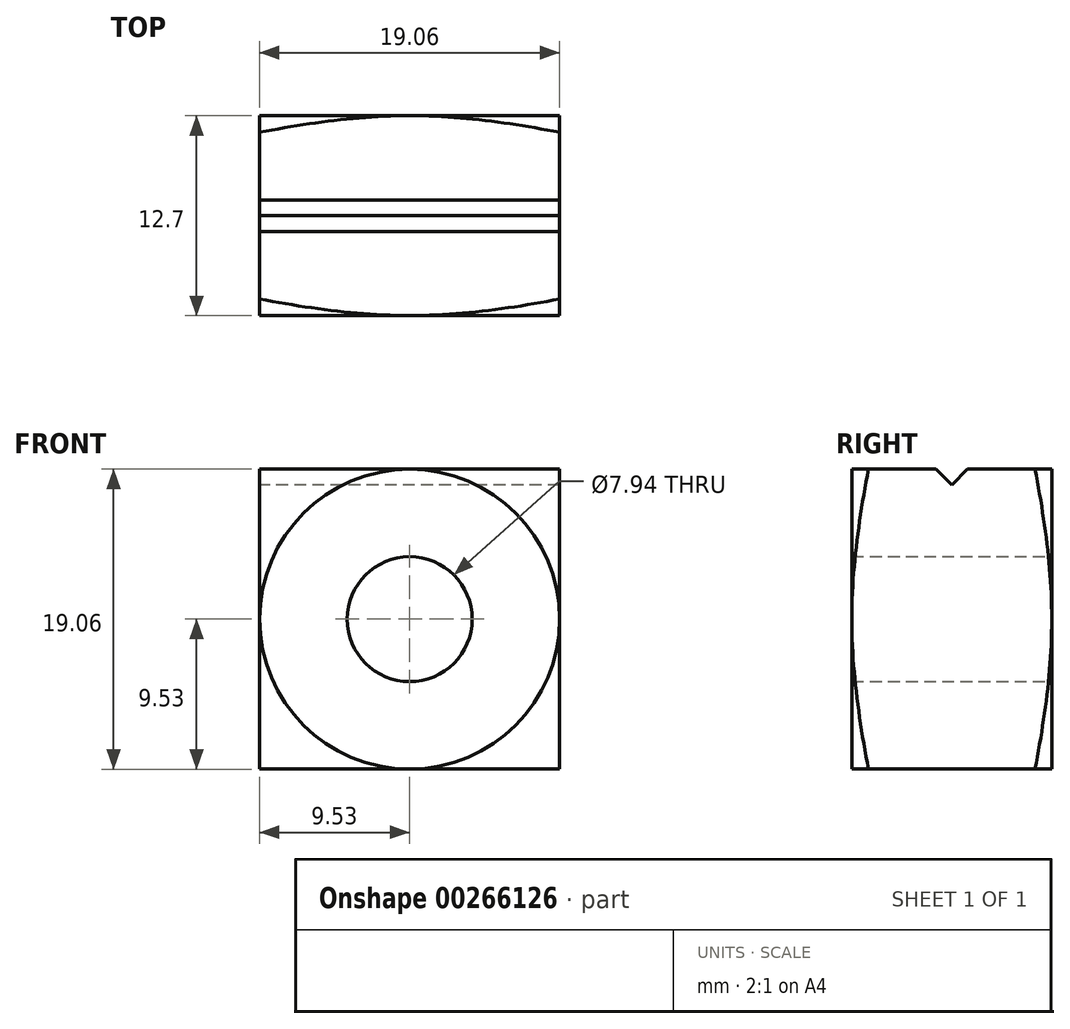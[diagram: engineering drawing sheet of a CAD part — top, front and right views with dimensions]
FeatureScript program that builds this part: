
annotation { "Feature Type Name" : "Feature", "Feature Type Description" : "" }
export const myFeature = defineFeature(function(context is Context, id is Id, definition is map)
    precondition{}
    {
        {
            var Q0;
            Q0=qCreatedBy(makeId("Front.planeOp"),FACE);
            var sketch = newSketch(context, id + "F0", { "sketchPlane" : qUnion([Q0])});
            skCircle(sketch, "E0", {"center": v(0, 0) * mm, "radius": 3.97 * mm});
            skCircle(sketch, "E1", {"center": v(0, 0) * mm, "radius": 9.53 * mm});
            skCircle(sketch, "E2.cCircle", {"center": v(0, 0) * mm, "radius": 9.53 * mm, "construction": true});
            skLineSegment(sketch, "E2.0", {"start": v(9.53, 9.53) * mm, "end": v(9.53, -9.53) * mm});
            skLineSegment(sketch, "E2.1", {"start": v(9.53, -9.53) * mm, "end": v(-9.53, -9.52) * mm});
            skLineSegment(sketch, "E2.2", {"start": v(-9.53, -9.53) * mm, "end": v(-9.53, 9.53) * mm});
            skLineSegment(sketch, "E2.3", {"start": v(-9.53, 9.53) * mm, "end": v(9.53, 9.53) * mm});
            skPoint(sketch, "E2.0.midPoint", {"position": v(9.52, 0) * mm});
            skSolve(sketch);
        }
        {
            var Q0;
            Q0 = qSketchRegion(id + "F0", true);
            extrude(context, id + "F1", {"entities" : qUnion([Q0]), "depth" : 12.7 * mm});
        }
        {
            var Q0;
            Q0=makeQuery(id+"F1.opExtrude","SWEPT_FACE",FACE,{"disambiguationData":[OSD([sQuery(id+"F0.wireOp",EDGE,"E2.0")])]});
            var Q1;
            Q1=makeQuery(id+"F1.opExtrude","SWEPT_FACE",FACE,{"disambiguationData":[OSD([sQuery(id+"F0.wireOp",EDGE,"E2.2")])]});
            cPlane(context, id + "F2", {"entities" : qUnion([Q0, Q1]), "cplaneType" : CPlaneType.MID_PLANE, "offset" : 25.4 * mm, "width" : 152.4 * mm, "height" : 152.4 * mm});
        }
        {
            var Q0;
            Q0=qCreatedBy(id+"F2.planeOp",FACE);
            var sketch = newSketch(context, id + "F3", { "sketchPlane" : qUnion([Q0])});
            skLineSegment(sketch, "E3.0.0", {"start": v(0, -9.53) * mm, "end": v(0, 9.53) * mm});
            skLineSegment(sketch, "E3.0.1", {"start": v(0, 9.53) * mm, "end": v(-12.7, 9.53) * mm});
            skLineSegment(sketch, "E3.0.2", {"start": v(-12.7, 9.53) * mm, "end": v(-12.7, -9.53) * mm});
            skLineSegment(sketch, "E3.0.3", {"start": v(-12.7, -9.53) * mm, "end": v(0, -9.53) * mm});
            skSolve(sketch);
        }
        {
            var Q0;
            Q0=makeQuery(id+"F1.opExtrude","SWEPT_FACE",FACE,{"disambiguationData":[OSD([sQuery(id+"F0.wireOp",EDGE,"E2.2")])]});
            var sketch = newSketch(context, id + "F4", { "sketchPlane" : qUnion([Q0])});
            skLineSegment(sketch, "E4", {"start": v(6.35, 9.52) * mm, "end": v(6.35, -9.53) * mm, "construction": true});
            skLineSegment(sketch, "E5", {"start": v(6.35, 8.52) * mm, "end": v(3.61, 11.26) * mm});
            skLineSegment(sketch, "E6", {"start": v(3.61, 11.26) * mm, "end": v(9.09, 11.26) * mm});
            skLineSegment(sketch, "E7", {"start": v(9.09, 11.26) * mm, "end": v(6.35, 8.52) * mm});
            skSolve(sketch);
        }
        {
            var Q0;
            Q0 = qSketchRegion(id + "F4", true);
            extrude(context, id + "F5", {"entities" : qUnion([Q0]), "operationType" : NewBodyOperationType.REMOVE, "oppositeDirection" : true, "depth" : 127 * mm});
        }
        {
            var Q0;
            Q0=makeQuery(id+"F3.imprint","IMPRINT",FACE,{"disambiguationData":[TD([[makeQuery(id+"F3.imprint","IMPRINT",EDGE,{"derivedFrom":sQuery(id+"F3.wireOp",EDGE,"E3.0.0")}),1.0]])]});
            var sketch = newSketch(context, id + "F6", { "sketchPlane" : qUnion([Q0])});
            skLineSegment(sketch, "E8.0.0", {"start": v(-5.35, 9.53) * mm, "end": v(-6.35, 8.52) * mm});
            skLineSegment(sketch, "E8.0.1", {"start": v(-6.35, 8.52) * mm, "end": v(-7.35, 9.53) * mm});
            skLineSegment(sketch, "E8.0.2", {"start": v(-7.35, 9.53) * mm, "end": v(-12.7, 9.53) * mm});
            skLineSegment(sketch, "E8.0.3", {"start": v(-12.7, 9.53) * mm, "end": v(-12.7, -9.53) * mm});
            skLineSegment(sketch, "E8.0.4", {"start": v(-12.7, -9.53) * mm, "end": v(0, -9.53) * mm});
            skLineSegment(sketch, "E8.0.5", {"start": v(0, -9.53) * mm, "end": v(0, 9.53) * mm});
            skLineSegment(sketch, "E8.0.6", {"start": v(0, 9.53) * mm, "end": v(-5.35, 9.53) * mm});
            skLineSegment(sketch, "E9", {"start": v(-12.7, 9.53) * mm, "end": v(-12.7, 15.63) * mm});
            skLineSegment(sketch, "E10", {"start": v(-12.7, 15.63) * mm, "end": v(-11.07, 15.63) * mm});
            skLineSegment(sketch, "E11", {"start": v(-11.07, 15.63) * mm, "end": v(-12.7, 9.53) * mm});
            skSolve(sketch);
        }
        {
            var Q0;
            Q0=makeQuery(id+"F6.imprint","IMPRINT",FACE,{"disambiguationData":[TD([[makeQuery(id+"F6.imprint","IMPRINT",EDGE,{"derivedFrom":sQuery(id+"F6.wireOp",EDGE,"E9")}),-1.0]])]});
            var Q1;
            Q1=makeQuery(id+"F1.opExtrude","SWEPT_FACE",FACE,{"disambiguationData":[OSD([sQuery(id+"F0.wireOp",EDGE,"E0")])]});
            revolve(context, id + "F7", {"operationType" : NewBodyOperationType.REMOVE, "entities" : qUnion([Q0]), "axis" : qUnion([Q1]), "revolveType" : RevolveType.FULL, "oppositeDirection" : true});
        }
        {
            var Q0;
            Q0=makeQuery(id+"F3.imprint","IMPRINT",FACE,{"disambiguationData":[TD([[makeQuery(id+"F3.imprint","IMPRINT",EDGE,{"derivedFrom":sQuery(id+"F3.wireOp",EDGE,"E3.0.0")}),1.0]])]});
            var sketch = newSketch(context, id + "F8", { "sketchPlane" : qUnion([Q0])});
            skLineSegment(sketch, "E12", {"start": v(0, 9.54) * mm, "end": v(0, 13.91) * mm});
            skLineSegment(sketch, "E13", {"start": v(0, 13.91) * mm, "end": v(-1.17, 13.91) * mm});
            skLineSegment(sketch, "E14", {"start": v(-1.17, 13.91) * mm, "end": v(0, 9.54) * mm});
            skSolve(sketch);
        }
        {
            var Q0;
            Q0=makeQuery(id+"F8.imprint","IMPRINT",FACE,{"disambiguationData":[TD([[makeQuery(id+"F8.imprint","IMPRINT",EDGE,{"derivedFrom":sQuery(id+"F8.wireOp",EDGE,"E12")}),1.0]])]});
            var Q1;
            Q1=makeQuery(id+"F1.opExtrude","CAP_EDGE",EDGE,{"disambiguationData":[OSD([sQuery(id+"F0.wireOp",EDGE,"E0")])],"isStart":true});
            revolve(context, id + "F9", {"operationType" : NewBodyOperationType.REMOVE, "entities" : qUnion([Q0]), "axis" : qUnion([Q1]), "revolveType" : RevolveType.FULL, "oppositeDirection" : true});
        }
    });
